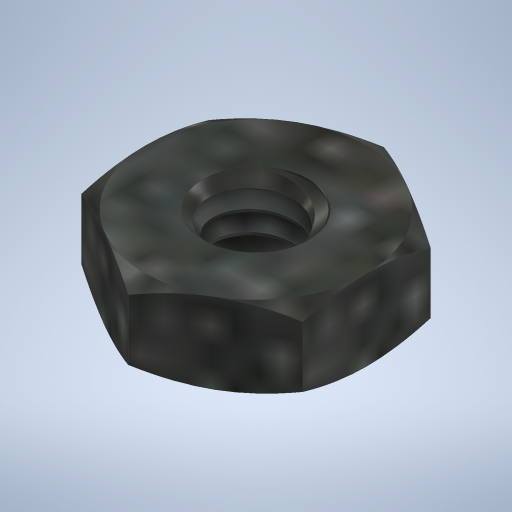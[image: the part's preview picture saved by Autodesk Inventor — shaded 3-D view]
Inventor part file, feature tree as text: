
AUTODESK INVENTOR PART (.ipt)
format: ipt  version: 2024 (Build 280153000, 153)  size: 448,000 bytes
history: native  units: in
note: dims shown in document units (in); Inventor stores cm internally (conversion verified against a paired STEP export)
features: mirror x1
ambient origin geometry x8: Origin, YZ Plane, XZ Plane, XY Plane, X Axis, Y Axis, Z Axis, Center Point
bodies: Solid1 (feature_tree)
feature tree (1):
  mirror  "Mirror1"
